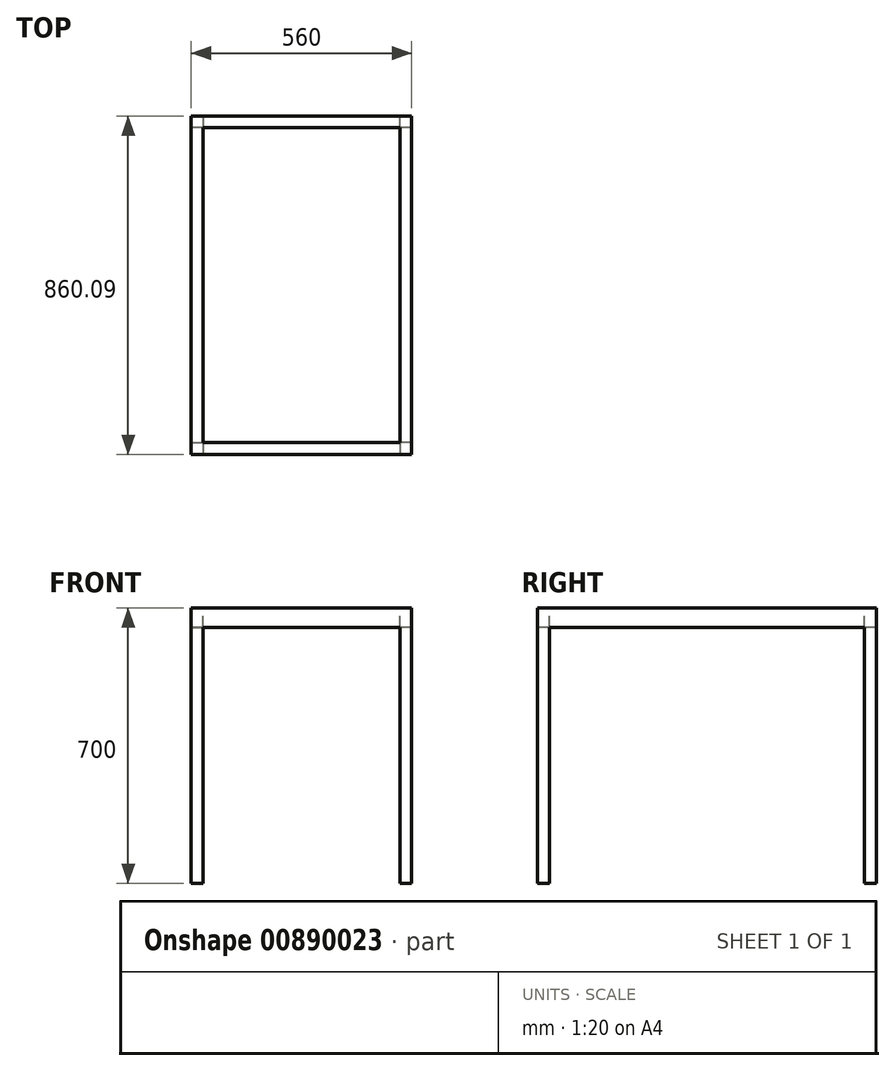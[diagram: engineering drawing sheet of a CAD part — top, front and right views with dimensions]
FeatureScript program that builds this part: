
annotation { "Feature Type Name" : "Feature", "Feature Type Description" : "" }
export const myFeature = defineFeature(function(context is Context, id is Id, definition is map)
    precondition{}
    {
        {
            var Q0;
            Q0=qCreatedBy(makeId("Top.planeOp"),FACE);
            var sketch = newSketch(context, id + "F0", { "sketchPlane" : qUnion([Q0])});
            skLineSegment(sketch, "E0.bottom", {"start": v(0, 0) * mm, "end": v(-500, 0) * mm});
            skLineSegment(sketch, "E0.top", {"start": v(0, 800) * mm, "end": v(-500, 800) * mm});
            skLineSegment(sketch, "E0.left", {"start": v(0, 0) * mm, "end": v(0, 800) * mm});
            skLineSegment(sketch, "E0.right", {"start": v(-500, 0) * mm, "end": v(-500, 800) * mm});
            skLineSegment(sketch, "E1", {"start": v(0, 0) * mm, "end": v(0, -30) * mm});
            skLineSegment(sketch, "E2", {"start": v(0, -30) * mm, "end": v(30, -30) * mm});
            skLineSegment(sketch, "E3", {"start": v(30, -30) * mm, "end": v(30, 0) * mm});
            skLineSegment(sketch, "E4", {"start": v(30, 0) * mm, "end": v(0, 0) * mm});
            skLineSegment(sketch, "E5", {"start": v(0, 800) * mm, "end": v(0, 830) * mm});
            skLineSegment(sketch, "E6", {"start": v(0, 830) * mm, "end": v(30, 830) * mm});
            skLineSegment(sketch, "E7", {"start": v(30, 830) * mm, "end": v(30, 800) * mm});
            skLineSegment(sketch, "E8", {"start": v(30, 800) * mm, "end": v(0, 800) * mm});
            skLineSegment(sketch, "E9", {"start": v(-500, 0) * mm, "end": v(-499.91, -30) * mm});
            skLineSegment(sketch, "E10", {"start": v(-499.91, -30) * mm, "end": v(-529.91, -30.09) * mm});
            skLineSegment(sketch, "E11", {"start": v(-529.91, -30.09) * mm, "end": v(-530, 0) * mm});
            skLineSegment(sketch, "E12", {"start": v(-530, 0) * mm, "end": v(-500, 0) * mm});
            skLineSegment(sketch, "E13", {"start": v(-500, 800) * mm, "end": v(-529.91, 800) * mm});
            skLineSegment(sketch, "E14", {"start": v(-529.91, 800) * mm, "end": v(-530, 830) * mm});
            skLineSegment(sketch, "E15", {"start": v(-530, 830) * mm, "end": v(-500, 830) * mm});
            skLineSegment(sketch, "E16", {"start": v(-500, 830) * mm, "end": v(-500, 800) * mm});
            skLineSegment(sketch, "E17", {"start": v(-500, 830) * mm, "end": v(0, 830) * mm});
            skLineSegment(sketch, "E18", {"start": v(-529.91, 800) * mm, "end": v(-530, 0) * mm});
            skLineSegment(sketch, "E19", {"start": v(-499.91, -30) * mm, "end": v(0, -30) * mm});
            skLineSegment(sketch, "E20", {"start": v(30, 0) * mm, "end": v(30, 800) * mm});
            skSolve(sketch);
        }
        {
            var Q0;
            Q0=makeQuery(id+"F0.imprint","IMPRINT",FACE,{"disambiguationData":[TD([[makeQuery(id+"F0.imprint","IMPRINT",EDGE,{"derivedFrom":sQuery(id+"F0.wireOp",EDGE,"E0.right")}),1.0]])]});
            var Q1;
            Q1=makeQuery(id+"F0.imprint","IMPRINT",FACE,{"disambiguationData":[TD([[makeQuery(id+"F0.imprint","IMPRINT",EDGE,{"derivedFrom":sQuery(id+"F0.wireOp",EDGE,"E13")}),-1.0]])]});
            var Q2;
            Q2=makeQuery(id+"F0.imprint","IMPRINT",FACE,{"disambiguationData":[TD([[makeQuery(id+"F0.imprint","IMPRINT",EDGE,{"derivedFrom":sQuery(id+"F0.wireOp",EDGE,"E0.top")}),-1.0]])]});
            var Q3;
            Q3=makeQuery(id+"F0.imprint","IMPRINT",FACE,{"disambiguationData":[TD([[makeQuery(id+"F0.imprint","IMPRINT",EDGE,{"derivedFrom":sQuery(id+"F0.wireOp",EDGE,"E5")}),-1.0]])]});
            var Q4;
            Q4=makeQuery(id+"F0.imprint","IMPRINT",FACE,{"disambiguationData":[TD([[makeQuery(id+"F0.imprint","IMPRINT",EDGE,{"derivedFrom":sQuery(id+"F0.wireOp",EDGE,"E0.left")}),-1.0]])]});
            var Q5;
            Q5=makeQuery(id+"F0.imprint","IMPRINT",FACE,{"disambiguationData":[TD([[makeQuery(id+"F0.imprint","IMPRINT",EDGE,{"derivedFrom":sQuery(id+"F0.wireOp",EDGE,"E1")}),1.0]])]});
            var Q6;
            Q6=makeQuery(id+"F0.imprint","IMPRINT",FACE,{"disambiguationData":[TD([[makeQuery(id+"F0.imprint","IMPRINT",EDGE,{"derivedFrom":sQuery(id+"F0.wireOp",EDGE,"E0.bottom")}),1.0]])]});
            var Q7;
            Q7=makeQuery(id+"F0.imprint","IMPRINT",FACE,{"disambiguationData":[TD([[makeQuery(id+"F0.imprint","IMPRINT",EDGE,{"derivedFrom":sQuery(id+"F0.wireOp",EDGE,"E9")}),-1.0]])]});
            extrude(context, id + "F1", {"entities" : qUnion([Q0, Q1, Q2, Q3, Q4, Q5, Q6, Q7]), "oppositeDirection" : true, "depth" : 50 * mm, "offsetDistance" : 25 * mm});
        }
        {
            var Q0;
            Q0=makeQuery(id+"F0.imprint","IMPRINT",FACE,{"disambiguationData":[TD([[makeQuery(id+"F0.imprint","IMPRINT",EDGE,{"derivedFrom":sQuery(id+"F0.wireOp",EDGE,"E1")}),1.0]])]});
            var Q1;
            Q1=makeQuery(id+"F0.imprint","IMPRINT",FACE,{"disambiguationData":[TD([[makeQuery(id+"F0.imprint","IMPRINT",EDGE,{"derivedFrom":sQuery(id+"F0.wireOp",EDGE,"E9")}),-1.0]])]});
            var Q2;
            Q2=makeQuery(id+"F0.imprint","IMPRINT",FACE,{"disambiguationData":[TD([[makeQuery(id+"F0.imprint","IMPRINT",EDGE,{"derivedFrom":sQuery(id+"F0.wireOp",EDGE,"E13")}),-1.0]])]});
            var Q3;
            Q3=makeQuery(id+"F0.imprint","IMPRINT",FACE,{"disambiguationData":[TD([[makeQuery(id+"F0.imprint","IMPRINT",EDGE,{"derivedFrom":sQuery(id+"F0.wireOp",EDGE,"E5")}),-1.0]])]});
            extrude(context, id + "F2", {"entities" : qUnion([Q0, Q1, Q2, Q3]), "operationType" : NewBodyOperationType.ADD, "oppositeDirection" : true, "depth" : 700 * mm, "offsetDistance" : 25 * mm});
        }
    });
